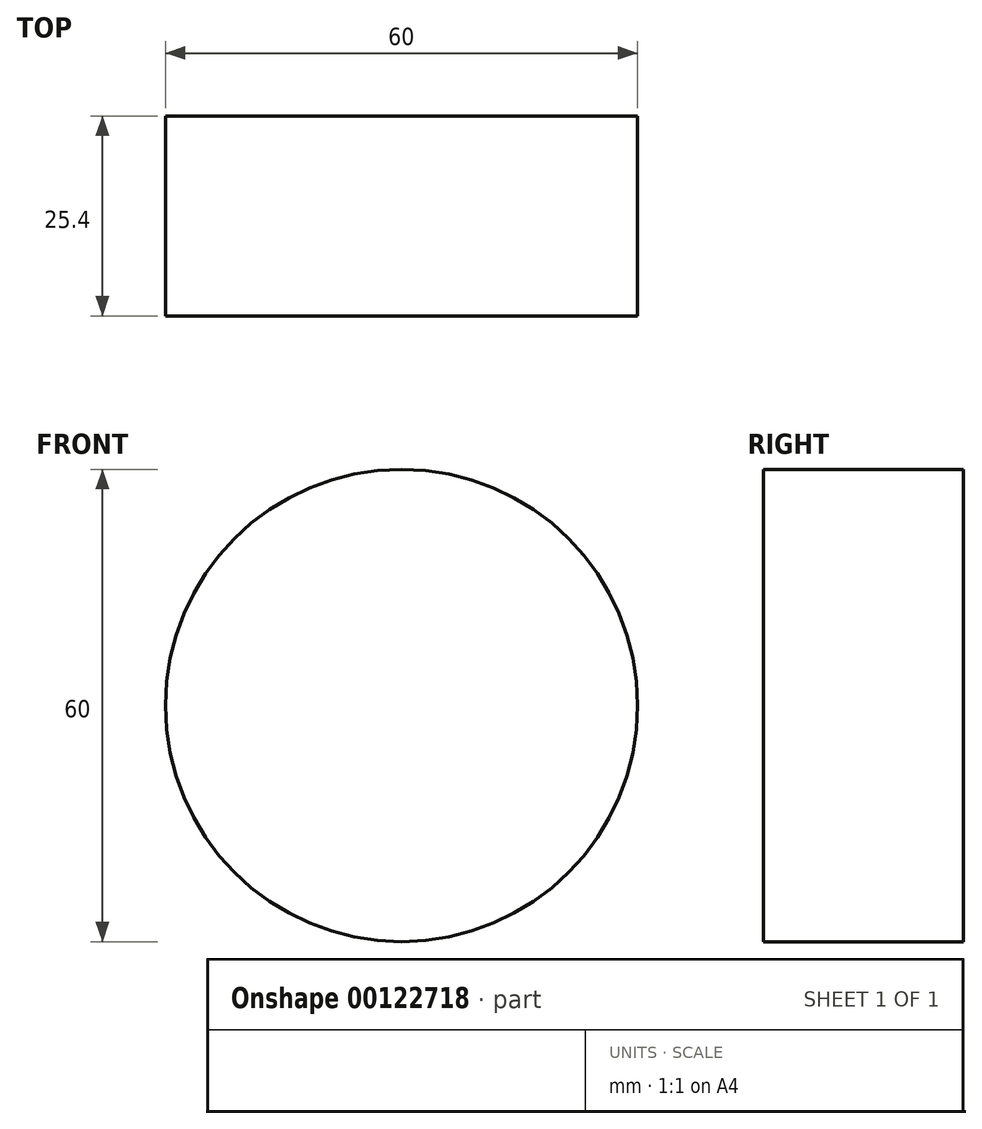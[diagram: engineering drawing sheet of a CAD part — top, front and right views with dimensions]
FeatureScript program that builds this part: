
annotation { "Feature Type Name" : "Feature", "Feature Type Description" : "" }
export const myFeature = defineFeature(function(context is Context, id is Id, definition is map)
    precondition{}
    {
        {
            var Q0;
            Q0=qCreatedBy(makeId("Front.planeOp"),FACE);
            var sketch = newSketch(context, id + "F0", { "sketchPlane" : qUnion([Q0])});
            skCircle(sketch, "E0", {"center": v(0, 0) * mm, "radius": 30 * mm});
            skSolve(sketch);
        }
        {
            var Q0;
            Q0=makeQuery(id+"F0.imprint","IMPRINT",FACE,{"disambiguationData":[TD([[makeQuery(id+"F0.imprint","IMPRINT",EDGE,{"derivedFrom":sQuery(id+"F0.wireOp",EDGE,"E0")}),1.0]])]});
            extrude(context, id + "F1", {"entities" : qUnion([Q0]), "endBound" : BoundingType.SYMMETRIC, "depth" : 25.4 * mm});
        }
    });
